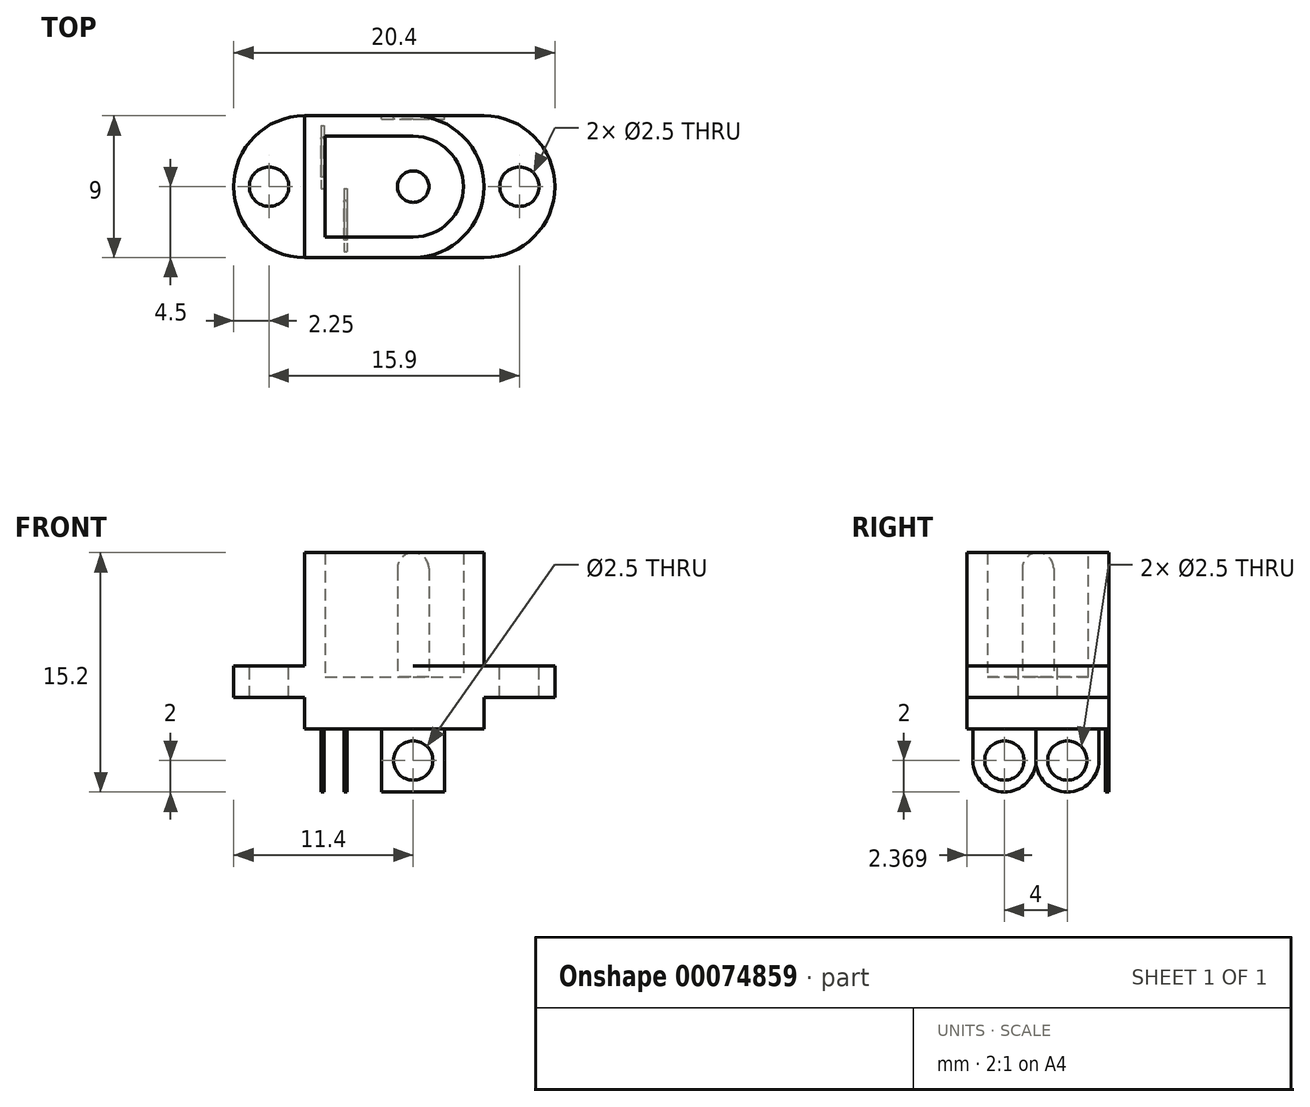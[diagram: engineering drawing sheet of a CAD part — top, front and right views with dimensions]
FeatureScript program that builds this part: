
annotation { "Feature Type Name" : "Feature", "Feature Type Description" : "" }
export const myFeature = defineFeature(function(context is Context, id is Id, definition is map)
    precondition{}
    {
        {
            var Q0;
            Q0=qCreatedBy(makeId("Top.planeOp"),FACE);
            var sketch = newSketch(context, id + "F0", { "sketchPlane" : qUnion([Q0])});
            skLineSegment(sketch, "E0.bottom", {"start": v(4.5, 0) * mm, "end": v(15.9, 0) * mm});
            skLineSegment(sketch, "E0.top", {"start": v(4.5, 9) * mm, "end": v(15.9, 9) * mm});
            skLineSegment(sketch, "E0.left", {"start": v(0, 4.5) * mm, "end": v(0, 4.5) * mm});
            skLineSegment(sketch, "E0.right", {"start": v(20.4, 4.5) * mm, "end": v(20.4, 4.5) * mm});
            skPoint(sketch, "E1.visualSharp", {"position": v(20.4, 9) * mm});
            skArc(sketch, "E1.filletArc", {"start": v(20.4, 4.5) * mm, "mid": v(19.08, 7.68) * mm, "end": v(15.9, 9) * mm});
            skPoint(sketch, "E2.visualSharp", {"position": v(0, 9) * mm});
            skArc(sketch, "E2.filletArc", {"start": v(4.5, 9) * mm, "mid": v(1.32, 7.68) * mm, "end": v(0, 4.5) * mm});
            skPoint(sketch, "E3.visualSharp", {"position": v(0, 0) * mm});
            skArc(sketch, "E3.filletArc", {"start": v(0, 4.5) * mm, "mid": v(1.32, 1.32) * mm, "end": v(4.5, 0) * mm});
            skPoint(sketch, "E4.visualSharp", {"position": v(20.4, 0) * mm});
            skArc(sketch, "E4.filletArc", {"start": v(15.9, 0) * mm, "mid": v(19.08, 1.32) * mm, "end": v(20.4, 4.5) * mm});
            skSolve(sketch);
        }
        {
            var Q0;
            Q0=makeQuery(id+"F0.imprint","IMPRINT",FACE,{"disambiguationData":[TD([[makeQuery(id+"F0.imprint","IMPRINT",EDGE,{"derivedFrom":sQuery(id+"F0.wireOp",EDGE,"E0.bottom")}),1.0]])]});
            extrude(context, id + "F1", {"entities" : qUnion([Q0]), "depth" : 2 * mm});
        }
        {
            var Q0;
            Q0=makeQuery(id+"F1.opExtrude","CAP_FACE",FACE,{"disambiguationData":[OSD([sQuery(id+"F0.wireOp",EDGE,"E0.bottom"),sQuery(id+"F0.wireOp",EDGE,"E0.top"),sQuery(id+"F0.wireOp",EDGE,"E1.filletArc"),sQuery(id+"F0.wireOp",EDGE,"E2.filletArc"),sQuery(id+"F0.wireOp",EDGE,"E3.filletArc"),sQuery(id+"F0.wireOp",EDGE,"E4.filletArc")])],"isStart":false});
            var sketch = newSketch(context, id + "F2", { "sketchPlane" : qUnion([Q0])});
            skLineSegment(sketch, "E5.bottom", {"start": v(4.5, 0) * mm, "end": v(11.4, 0) * mm});
            skLineSegment(sketch, "E5.top", {"start": v(4.5, 9) * mm, "end": v(11.4, 9) * mm});
            skLineSegment(sketch, "E5.left", {"start": v(4.5, 0) * mm, "end": v(4.5, 9) * mm});
            skLineSegment(sketch, "E5.right", {"start": v(15.9, 4.5) * mm, "end": v(15.9, 4.5) * mm});
            skPoint(sketch, "E6.visualSharp", {"position": v(15.9, 0) * mm});
            skArc(sketch, "E6.filletArc", {"start": v(11.4, 0) * mm, "mid": v(14.58, 1.32) * mm, "end": v(15.9, 4.5) * mm});
            skPoint(sketch, "E7.visualSharp", {"position": v(15.9, 9) * mm});
            skArc(sketch, "E7.filletArc", {"start": v(15.9, 4.5) * mm, "mid": v(14.58, 7.68) * mm, "end": v(11.4, 9) * mm});
            skSolve(sketch);
        }
        {
            var Q0;
            Q0=makeQuery(id+"F2.imprint","IMPRINT",FACE,{"disambiguationData":[TD([[makeQuery(id+"F2.imprint","IMPRINT",EDGE,{"derivedFrom":sQuery(id+"F2.wireOp",EDGE,"E5.bottom")}),1.0]])]});
            extrude(context, id + "F3", {"entities" : qUnion([Q0]), "operationType" : NewBodyOperationType.ADD, "depth" : 7.2 * mm});
        }
        {
            var Q0;
            Q0=makeQuery(id+"F3.opExtrude","CAP_FACE",FACE,{"disambiguationData":[OSD([sQuery(id+"F2.wireOp",EDGE,"E5.bottom"),sQuery(id+"F2.wireOp",EDGE,"E5.top"),sQuery(id+"F2.wireOp",EDGE,"E5.left"),sQuery(id+"F2.wireOp",EDGE,"E6.filletArc"),sQuery(id+"F2.wireOp",EDGE,"E7.filletArc")])],"isStart":false});
            shell(context, id + "F4", {"entities" : qUnion([Q0]), "thickness" : 1.3 * mm});
        }
        {
            var Q0;
            Q0=makeQuery(id+"F4.opShell","OFFSET_FACE",FACE,{"disambiguationData":[OSD([sQuery(id+"F0.wireOp",EDGE,"E0.bottom"),sQuery(id+"F0.wireOp",EDGE,"E0.top"),sQuery(id+"F0.wireOp",EDGE,"E1.filletArc"),sQuery(id+"F0.wireOp",EDGE,"E2.filletArc"),sQuery(id+"F0.wireOp",EDGE,"E3.filletArc"),sQuery(id+"F0.wireOp",EDGE,"E4.filletArc")])]});
            var sketch = newSketch(context, id + "F5", { "sketchPlane" : qUnion([Q0])});
            skCircle(sketch, "E8", {"center": v(11.4, 4.5) * mm, "radius": 1 * mm});
            skSolve(sketch);
        }
        {
            var Q0;
            Q0=makeQuery(id+"F5.imprint","IMPRINT",FACE,{"disambiguationData":[TD([[makeQuery(id+"F5.imprint","IMPRINT",EDGE,{"derivedFrom":sQuery(id+"F5.wireOp",EDGE,"E8")}),1.0]])]});
            var Q1;
            Q1=makeQuery(id+"F3.opExtrude","CAP_FACE",FACE,{"disambiguationData":[OSD([sQuery(id+"F2.wireOp",EDGE,"E5.bottom"),sQuery(id+"F2.wireOp",EDGE,"E5.top"),sQuery(id+"F2.wireOp",EDGE,"E5.left"),sQuery(id+"F2.wireOp",EDGE,"E6.filletArc"),sQuery(id+"F2.wireOp",EDGE,"E7.filletArc")])],"isStart":false});
            var Q2;
            Q2=makeQuery(id+"F1.opExtrude","SWEPT_BODY",BODY,{"disambiguationData":[OSD([sQuery(id+"F0.wireOp",EDGE,"E0.bottom"),sQuery(id+"F0.wireOp",EDGE,"E0.top"),sQuery(id+"F0.wireOp",EDGE,"E1.filletArc"),sQuery(id+"F0.wireOp",EDGE,"E2.filletArc"),sQuery(id+"F0.wireOp",EDGE,"E3.filletArc"),sQuery(id+"F0.wireOp",EDGE,"E4.filletArc")])]});
            extrude(context, id + "F6", {"entities" : qUnion([Q0]), "operationType" : NewBodyOperationType.ADD, "endBound" : BoundingType.UP_TO_SURFACE, "endBoundEntityFace" : qUnion([Q1]), "endBoundEntityBody" : qUnion([Q2]), "depth" : 9.43 * mm});
        }
        {
            var Q0;
            Q0=makeQuery(id+"F6.opExtrude","CAP_EDGE",EDGE,{"disambiguationData":[OSD([sQuery(id+"F5.wireOp",EDGE,"E8")])],"isStart":false});
            fillet(context, id + "F7", {"entities" : qUnion([Q0]), "radius" : 1 * mm, "tangentPropagation" : true, "allowEdgeOverflow" : false});
        }
        {
            var Q0;
            {var subQ0=sQuery(id+"F0.wireOp",EDGE,"E3.filletArc");var subQ1=sQuery(id+"F0.wireOp",EDGE,"E2.filletArc");var subQ2=sQuery(id+"F0.wireOp",EDGE,"E0.top");var subQ3=sQuery(id+"F0.wireOp",EDGE,"E0.bottom");Q0=makeQuery(id+"F3.boolean.opBoolean","SPLIT",FACE,{"disambiguationData":[TD([makeQuery(id+"F3.opExtrude","SWEPT_FACE",FACE,{"disambiguationData":[OSD([sQuery(id+"F2.wireOp",EDGE,"E5.left")])]})])],"derivedFrom":makeQuery(id+"F1.opExtrude","CAP_FACE",FACE,{"disambiguationData":[OSD([subQ3,subQ2,sQuery(id+"F0.wireOp",EDGE,"E1.filletArc"),subQ1,subQ0,sQuery(id+"F0.wireOp",EDGE,"E4.filletArc")])],"isStart":false})});}
            var sketch = newSketch(context, id + "F8", { "sketchPlane" : qUnion([Q0])});
            skLineSegment(sketch, "E9", {"start": v(0, 4.5) * mm, "end": v(0, 10.1) * mm, "construction": true});
            skLineSegment(sketch, "E10.0", {"start": v(2.25, 4.5) * mm, "end": v(2.25, 10.1) * mm, "construction": true});
            skCircle(sketch, "E11", {"center": v(2.25, 4.5) * mm, "radius": 1.25 * mm});
            skSolve(sketch);
        }
        {
            var Q0;
            Q0=makeQuery(id+"F8.imprint","IMPRINT",FACE,{"disambiguationData":[TD([[makeQuery(id+"F8.imprint","IMPRINT",EDGE,{"derivedFrom":sQuery(id+"F8.wireOp",EDGE,"E11")}),1.0]])]});
            extrude(context, id + "F9", {"entities" : qUnion([Q0]), "operationType" : NewBodyOperationType.REMOVE, "endBound" : BoundingType.THROUGH_ALL, "oppositeDirection" : true, "depth" : 25 * mm});
        }
        {
            var Q0;
            {var subQ0=sQuery(id+"F0.wireOp",EDGE,"E4.filletArc");var subQ1=sQuery(id+"F0.wireOp",EDGE,"E1.filletArc");var subQ2=sQuery(id+"F0.wireOp",EDGE,"E0.top");var subQ3=sQuery(id+"F0.wireOp",EDGE,"E0.bottom");Q0=makeQuery(id+"F3.boolean.opBoolean","SPLIT",FACE,{"disambiguationData":[TD([makeQuery(id+"F1.opExtrude","SWEPT_FACE",FACE,{"disambiguationData":[OSD([subQ1,subQ0])]})])],"derivedFrom":makeQuery(id+"F1.opExtrude","CAP_FACE",FACE,{"disambiguationData":[OSD([subQ3,subQ2,subQ1,sQuery(id+"F0.wireOp",EDGE,"E2.filletArc"),sQuery(id+"F0.wireOp",EDGE,"E3.filletArc"),subQ0])],"isStart":false})});}
            var sketch = newSketch(context, id + "F10", { "sketchPlane" : qUnion([Q0])});
            skLineSegment(sketch, "E12", {"start": v(20.4, 4.5) * mm, "end": v(20.4, 14.6) * mm, "construction": true});
            skLineSegment(sketch, "E13.0", {"start": v(18.15, 4.5) * mm, "end": v(18.15, 14.6) * mm, "construction": true});
            skCircle(sketch, "E14", {"center": v(18.15, 4.5) * mm, "radius": 1.25 * mm});
            skSolve(sketch);
        }
        {
            var Q0;
            Q0=makeQuery(id+"F10.imprint","IMPRINT",FACE,{"disambiguationData":[TD([[makeQuery(id+"F10.imprint","IMPRINT",EDGE,{"derivedFrom":sQuery(id+"F10.wireOp",EDGE,"E14")}),1.0]])]});
            extrude(context, id + "F11", {"entities" : qUnion([Q0]), "operationType" : NewBodyOperationType.REMOVE, "endBound" : BoundingType.THROUGH_ALL, "oppositeDirection" : true, "depth" : 25 * mm});
        }
        {
            var Q0;
            Q0=makeQuery(id+"F1.opExtrude","CAP_FACE",FACE,{"disambiguationData":[OSD([sQuery(id+"F0.wireOp",EDGE,"E0.bottom"),sQuery(id+"F0.wireOp",EDGE,"E0.top"),sQuery(id+"F0.wireOp",EDGE,"E1.filletArc"),sQuery(id+"F0.wireOp",EDGE,"E2.filletArc"),sQuery(id+"F0.wireOp",EDGE,"E3.filletArc"),sQuery(id+"F0.wireOp",EDGE,"E4.filletArc")])],"isStart":true});
            var sketch = newSketch(context, id + "F12", { "sketchPlane" : qUnion([Q0])});
            skLineSegment(sketch, "E15.bottom", {"start": v(4.5, 0) * mm, "end": v(15.9, 0) * mm});
            skLineSegment(sketch, "E15.top", {"start": v(4.5, -9) * mm, "end": v(15.9, -9) * mm});
            skLineSegment(sketch, "E15.left", {"start": v(4.5, 0) * mm, "end": v(4.5, -9) * mm});
            skLineSegment(sketch, "E15.right", {"start": v(15.9, 0) * mm, "end": v(15.9, -9) * mm});
            skSolve(sketch);
        }
        {
            var Q0;
            Q0=makeQuery(id+"F12.imprint","IMPRINT",FACE,{"disambiguationData":[TD([[makeQuery(id+"F12.imprint","IMPRINT",EDGE,{"derivedFrom":sQuery(id+"F12.wireOp",EDGE,"E15.bottom")}),-1.0]])]});
            extrude(context, id + "F13", {"entities" : qUnion([Q0]), "operationType" : NewBodyOperationType.ADD, "depth" : 2 * mm});
        }
        {
            var Q0;
            Q0=makeQuery(id+"F13.opExtrude","CAP_FACE",FACE,{"disambiguationData":[OSD([sQuery(id+"F12.wireOp",EDGE,"E15.bottom"),sQuery(id+"F12.wireOp",EDGE,"E15.top"),sQuery(id+"F12.wireOp",EDGE,"E15.left"),sQuery(id+"F12.wireOp",EDGE,"E15.right")])],"isStart":false});
            var sketch = newSketch(context, id + "F14", { "sketchPlane" : qUnion([Q0])});
            skLineSegment(sketch, "E16", {"start": v(4.5, -4.5) * mm, "end": v(15.9, -4.5) * mm, "construction": true});
            skLineSegment(sketch, "E17.0", {"start": v(11.4, 0) * mm, "end": v(11.4, -9) * mm, "construction": true});
            skCircle(sketch, "E18", {"center": v(11.4, -4.5) * mm, "radius": 2 * mm});
            skLineSegment(sketch, "E19", {"start": v(13.4, -4.5) * mm, "end": v(13.4, -9) * mm});
            skLineSegment(sketch, "E20", {"start": v(9.4, -4.5) * mm, "end": v(9.4, -9) * mm});
            skLineSegment(sketch, "E21", {"start": v(9.4, -9) * mm, "end": v(13.4, -9) * mm});
            skLineSegment(sketch, "E22.top", {"start": v(9.4, -8.8) * mm, "end": v(13.4, -8.8) * mm});
            skLineSegment(sketch, "E22.left", {"start": v(9.4, -9) * mm, "end": v(9.4, -8.8) * mm});
            skLineSegment(sketch, "E22.right", {"start": v(13.4, -9) * mm, "end": v(13.4, -8.8) * mm});
            skLineSegment(sketch, "E23.bottom", {"start": v(5.55, -8.37) * mm, "end": v(5.75, -8.37) * mm});
            skLineSegment(sketch, "E23.top", {"start": v(5.55, -4.37) * mm, "end": v(5.75, -4.37) * mm});
            skLineSegment(sketch, "E23.left", {"start": v(5.55, -8.37) * mm, "end": v(5.55, -4.37) * mm});
            skLineSegment(sketch, "E23.right", {"start": v(5.75, -8.37) * mm, "end": v(5.75, -4.37) * mm});
            skLineSegment(sketch, "E24.bottom", {"start": v(7, -4.37) * mm, "end": v(7.2, -4.37) * mm});
            skLineSegment(sketch, "E24.top", {"start": v(7, -0.37) * mm, "end": v(7.2, -0.37) * mm});
            skLineSegment(sketch, "E24.left", {"start": v(7, -4.37) * mm, "end": v(7, -0.37) * mm});
            skLineSegment(sketch, "E24.right", {"start": v(7.2, -4.37) * mm, "end": v(7.2, -0.37) * mm});
            skSolve(sketch);
        }
        {
            var Q0;
            Q0=makeQuery(id+"F14.imprint","IMPRINT",FACE,{"disambiguationData":[TD([[makeQuery(id+"F14.imprint","IMPRINT",EDGE,{"derivedFrom":sQuery(id+"F14.wireOp",EDGE,"E24.bottom")}),1.0]])]});
            var Q1;
            Q1=makeQuery(id+"F14.imprint","IMPRINT",FACE,{"disambiguationData":[TD([[makeQuery(id+"F14.imprint","IMPRINT",EDGE,{"derivedFrom":sQuery(id+"F14.wireOp",EDGE,"E23.bottom")}),1.0]])]});
            var Q2;
            Q2=makeQuery(id+"F14.imprint","IMPRINT",FACE,{"disambiguationData":[TD([[makeQuery(id+"F14.imprint","IMPRINT",EDGE,{"derivedFrom":sQuery(id+"F14.wireOp",EDGE,"E21")}),1.0]])]});
            extrude(context, id + "F15", {"entities" : qUnion([Q0, Q1, Q2]), "operationType" : NewBodyOperationType.ADD, "depth" : 4 * mm});
        }
        {
            var Q0;
            Q0=makeQuery(id+"F15.opExtrude","CAP_EDGE",EDGE,{"disambiguationData":[OSD([sQuery(id+"F14.wireOp",EDGE,"E24.top")])],"isStart":false});
            var Q1;
            Q1=makeQuery(id+"F15.opExtrude","CAP_EDGE",EDGE,{"disambiguationData":[OSD([sQuery(id+"F14.wireOp",EDGE,"E23.top")])],"isStart":false});
            var Q2;
            Q2=makeQuery(id+"F15.opExtrude","CAP_EDGE",EDGE,{"disambiguationData":[OSD([sQuery(id+"F14.wireOp",EDGE,"E22.left")])],"isStart":false});
            var Q3;
            Q3=makeQuery(id+"F15.opExtrude","CAP_EDGE",EDGE,{"disambiguationData":[OSD([sQuery(id+"F14.wireOp",EDGE,"E22.right")])],"isStart":false});
            var Q4;
            Q4=makeQuery(id+"F15.opExtrude","CAP_EDGE",EDGE,{"disambiguationData":[OSD([sQuery(id+"F14.wireOp",EDGE,"E23.bottom")])],"isStart":false});
            var Q5;
            Q5=makeQuery(id+"F15.opExtrude","CAP_EDGE",EDGE,{"disambiguationData":[OSD([sQuery(id+"F14.wireOp",EDGE,"E24.bottom")])],"isStart":false});
            fillet(context, id + "F16", {"entities" : qUnion([Q0, Q1, Q2, Q3, Q4, Q5]), "radius" : 2 * mm, "tangentPropagation" : true, "allowEdgeOverflow" : false});
        }
        {
            var Q0;
            Q0=makeQuery(id+"F15.opExtrude","SWEPT_FACE",FACE,{"disambiguationData":[OSD([sQuery(id+"F14.wireOp",EDGE,"E24.left")])]});
            var sketch = newSketch(context, id + "F17", { "sketchPlane" : qUnion([Q0])});
            skCircle(sketch, "E25", {"center": v(-2.37, -4) * mm, "radius": 1.25 * mm});
            skSolve(sketch);
        }
        {
            var Q0;
            Q0=makeQuery(id+"F17.imprint","IMPRINT",FACE,{"disambiguationData":[TD([[makeQuery(id+"F17.imprint","IMPRINT",EDGE,{"derivedFrom":sQuery(id+"F17.wireOp",EDGE,"E25")}),1.0]])]});
            extrude(context, id + "F18", {"entities" : qUnion([Q0]), "operationType" : NewBodyOperationType.REMOVE, "oppositeDirection" : true, "depth" : 25 * mm});
        }
        {
            var Q0;
            Q0=makeQuery(id+"F15.opExtrude","SWEPT_FACE",FACE,{"disambiguationData":[OSD([sQuery(id+"F14.wireOp",EDGE,"E23.left")])]});
            var sketch = newSketch(context, id + "F19", { "sketchPlane" : qUnion([Q0])});
            skCircle(sketch, "E26", {"center": v(-6.37, -4) * mm, "radius": 1.25 * mm});
            skSolve(sketch);
        }
        {
            var Q0;
            Q0=makeQuery(id+"F19.imprint","IMPRINT",FACE,{"disambiguationData":[TD([[makeQuery(id+"F19.imprint","IMPRINT",EDGE,{"derivedFrom":sQuery(id+"F19.wireOp",EDGE,"E26")}),1.0]])]});
            extrude(context, id + "F20", {"entities" : qUnion([Q0]), "operationType" : NewBodyOperationType.REMOVE, "oppositeDirection" : true, "depth" : 25 * mm});
        }
        {
            var Q0;
            Q0=makeQuery(id+"F15.boolean.opBoolean","MERGE",FACE,{"derivedFrom":[makeQuery(id+"F13.boolean.opBoolean","MERGE",FACE,{"derivedFrom":[makeQuery(id+"F3.boolean.opBoolean","MERGE",FACE,{"derivedFrom":[makeQuery(id+"F1.opExtrude","SWEPT_FACE",FACE,{"disambiguationData":[OSD([sQuery(id+"F0.wireOp",EDGE,"E0.top")])]}),makeQuery(id+"F3.opExtrude","SWEPT_FACE",FACE,{"disambiguationData":[OSD([sQuery(id+"F2.wireOp",EDGE,"E5.top")])]})]}),makeQuery(id+"F13.opExtrude","SWEPT_FACE",FACE,{"disambiguationData":[OSD([sQuery(id+"F12.wireOp",EDGE,"E15.top")])]})]}),makeQuery(id+"F15.opExtrude","SWEPT_FACE",FACE,{"disambiguationData":[OSD([sQuery(id+"F14.wireOp",EDGE,"E21")])]})]});
            var sketch = newSketch(context, id + "F21", { "sketchPlane" : qUnion([Q0])});
            skCircle(sketch, "E27", {"center": v(-11.4, -4) * mm, "radius": 1.25 * mm});
            skSolve(sketch);
        }
        {
            var Q0;
            Q0=makeQuery(id+"F21.imprint","IMPRINT",FACE,{"disambiguationData":[TD([[makeQuery(id+"F21.imprint","IMPRINT",EDGE,{"derivedFrom":sQuery(id+"F21.wireOp",EDGE,"E27")}),1.0]])]});
            extrude(context, id + "F22", {"entities" : qUnion([Q0]), "operationType" : NewBodyOperationType.REMOVE, "oppositeDirection" : true, "depth" : 25 * mm});
        }
    });
